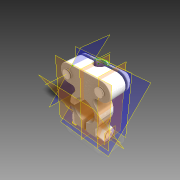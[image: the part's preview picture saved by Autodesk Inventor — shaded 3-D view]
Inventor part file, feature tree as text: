
AUTODESK INVENTOR PART (.ipt)
format: ipt  version: 2014 (Build 180170000, 170)  size: 776,192 bytes
history: native  units: in
note: dims shown in document units (in); Inventor stores cm internally (conversion verified against a paired STEP export)
features: sketch x15, projected_geometry x11, extrude x10, fillet x8, plane x8, revolve x4, other x4, thread x4, mirror x2, hole x1, chamfer x1, surface_op x1, reference x1
ambient origin geometry x8: Origin, YZ Plane, XZ Plane, XY Plane, X Axis, Y Axis, Z Axis, Center Point
bodies: Solid1 (feature_tree), Solid2 (feature_tree), Solid3 (feature_tree), Solid4 (feature_tree), Solid5 (feature_tree)
feature tree (70):
  extrude  "Extrusion1"  Depth=0.125in
  fillet  "Fillet1"  Radius=0.25in
  hole  "Hole1"  [1 undecoded]
  revolve  "Revolution1"  [1 undecoded]
  plane  "Work Plane1"
  extrude  "Extrusion2"  Depth=0.315in
  extrude  "Extrusion3"  Depth=0.0625in
  sketch  "Sketch6"  dims[d18=90.0deg d19=0.0625in]
  extrude  "Extrusion4"  Depth=0.0625in TaperAngle=0.0deg
  extrude  "Extrusion5"  Depth=0.0625in TaperAngle=0.0deg
  extrude  "Extrusion6"  TaperAngle=90.0deg  [1 undecoded]
  plane  "Work Plane2"
  sketch  "Sketch8"  dims[d24=0.0625in d25=0.0in d26=0.0625in d27=0.0in]
  other  "Work Axis1"
  revolve  "Revolution2"  [1 undecoded]
  fillet  "Fillet2"  Radius=0.2in
  fillet  "Fillet3"  [1 undecoded]
  extrude  "Extrusion7"  Depth=0.2in TaperAngle=0.0deg
  plane  "Work Plane3"
  revolve  "Revolution3"  Angle=45.0deg
  plane  "Work Plane4"
  mirror  "Mirror1"
  plane  "Work Plane5"
  extrude  "Extrusion8"  Depth=0.1375in TaperAngle=0.0deg
  thread  "Thread1"  [1 undecoded]
  chamfer  "Chamfer1"  Distance=0.01in
  thread  "Thread2"  [1 undecoded]
  thread  "Thread3"  [1 undecoded]
  extrude  "Extrusion9"  Depth=0.02in TaperAngle=0.0deg
  plane  "Work Plane6"
  sketch  "Sketch14"  dims[d50=90.0deg]
  other  "Work Axis2"
  revolve  "Revolution4"  [1 undecoded]
  fillet  "Fillet4"  Radius=0.02in
  fillet  "Fillet5"  Radius=0.02in
  plane  "Work Plane7"
  extrude  "Extrusion10"  [1 undecoded]
  thread  "Thread4"  [1 undecoded]
  plane  "Work Plane8"
  mirror  "Mirror2"
  fillet  "Fillet6"  [1 undecoded]
  fillet  "Fillet7"  [1 undecoded]
  fillet  "Fillet8"  [1 undecoded]
  surface_op  "Sculpt1"
  sketch  "Sketch1"  dims[d0=0.15in d1=0.125in d3=0.25in]
  reference  "Reference1"
  sketch  "Sketch2"  dims[d4=0.25in d5=0.2in]
  projected_geometry  "Projected Loop1"
  sketch  "Sketch3"  dims[d6=0.2in d7=0.5in d8=0.0in]
  projected_geometry  "Projected Loop2"
  sketch  "Sketch4"  dims[d9=0.2in]
  projected_geometry  "Projected Loop3"
  sketch  "Sketch5"  dims[d10=0.25in d11=0.75in d12=0.375in d13=0.25in d14=0.5635in d15=1.0in d16=0.8108in d17=0.315in]
  sketch  "Sketch7"  dims[d20=0.0625in d21=0.0in d22=0.0625in d23=0.0in]
  projected_geometry  "Projected Loop5"
  sketch  "Sketch9"  dims[d28=0.15in d29=0.0in d30=90.0deg]
  projected_geometry  "Projected Loop6"
  projected_geometry  "Projected Loop7"
  sketch  "Sketch10"  dims[d31=0.02in d32=0.01in d33=0.2in d34=0.0in d35=90.0deg]
  sketch  "Sketch11"  dims[d36=0.035in d37=0.2in d38=0.0in]
  projected_geometry  "Projected Loop8"
  projected_geometry  "Projected Loop9"
  sketch  "Sketch12"  dims[d39=1.0in d40=0.0in d41=0.02in d42=0.125in d43=45.0deg]
  sketch  "Sketch13"  dims[d44=1.0in d45=0.0in d46=1.0in d47=0.0in d48=0.1375in d49=0.0in]
  projected_geometry  "Projected Loop10"
  projected_geometry  "Projected Loop11"
  sketch  "Sketch15"  dims[d51=0.01in d52=0.01in d53=0.0625in d54=0.1375in d55=0.0in d56=1.0in d57=0.0in d58=0.1in d59=0.02in d60=0.02in]
  projected_geometry  "Project Cut Edges1"
  other  "Composite1"
  other  "Srf1"
note: 14 required parameter values undecoded (feature->parameter linkage not recoverable at this tier; creation-order binding heuristic only, values carry confidence <= 0.55)